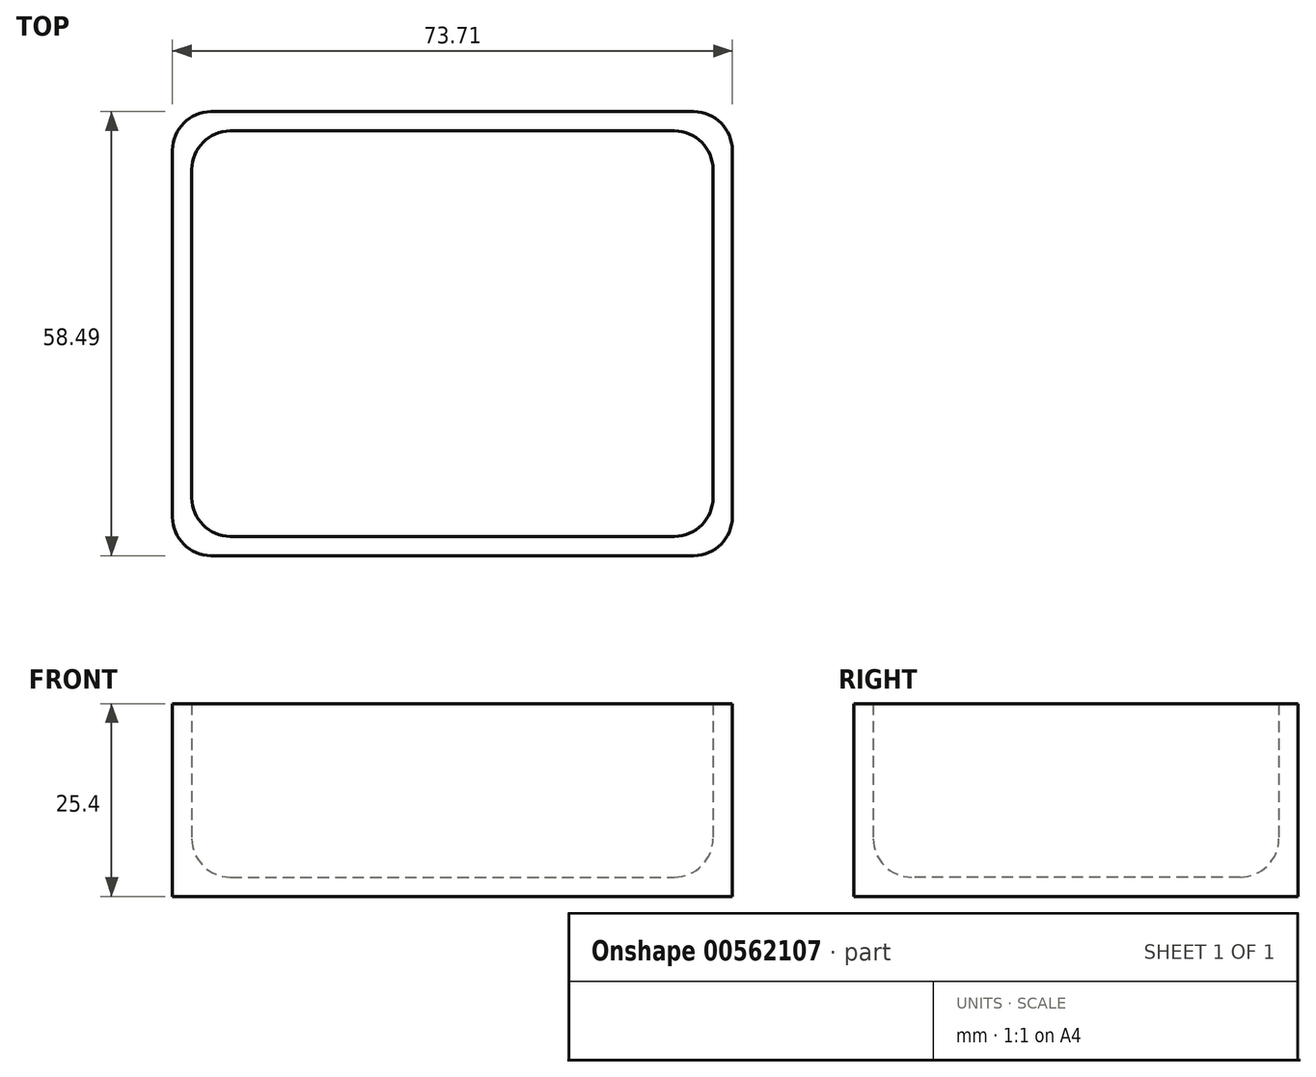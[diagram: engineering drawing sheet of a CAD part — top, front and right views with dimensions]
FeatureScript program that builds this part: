
annotation { "Feature Type Name" : "Feature", "Feature Type Description" : "" }
export const myFeature = defineFeature(function(context is Context, id is Id, definition is map)
    precondition{}
    {
        {
            var Q0;
            Q0=qCreatedBy(makeId("Top.planeOp"),FACE);
            var sketch = newSketch(context, id + "F0", { "sketchPlane" : qUnion([Q0])});
            skLineSegment(sketch, "E0.bottom", {"start": v(0, 0) * mm, "end": v(73.7, 0) * mm});
            skLineSegment(sketch, "E0.top", {"start": v(0, -58.49) * mm, "end": v(73.7, -58.49) * mm});
            skLineSegment(sketch, "E0.left", {"start": v(0, 0) * mm, "end": v(0, -58.49) * mm});
            skLineSegment(sketch, "E0.right", {"start": v(73.7, 0) * mm, "end": v(73.7, -58.49) * mm});
            skSolve(sketch);
        }
        {
            var Q0;
            Q0 = qSketchRegion(id + "F0", true);
            var Q1;
            Q1=makeQuery(id+"F0.imprint","IMPRINT",FACE,{"disambiguationData":[TD([[makeQuery(id+"F0.imprint","IMPRINT",EDGE,{"derivedFrom":sQuery(id+"F0.wireOp",EDGE,"E0.bottom")}),-1.0]])]});
            extrude(context, id + "F1", {"entities" : qUnion([Q0, Q1]), "depth" : 25.4 * mm, "offsetDistance" : 25.4 * mm});
        }
        {
            var Q0;
            Q0=makeQuery(id+"F1.opExtrude","CAP_FACE",FACE,{"disambiguationData":[OSD([sQuery(id+"F0.wireOp",EDGE,"E0.bottom"),sQuery(id+"F0.wireOp",EDGE,"E0.top"),sQuery(id+"F0.wireOp",EDGE,"E0.left"),sQuery(id+"F0.wireOp",EDGE,"E0.right")])],"isStart":false});
            shell(context, id + "F2", {"entities" : qUnion([Q0]), "thickness" : 2.54 * mm});
        }
        {
            var Q0;
            Q0=makeQuery(id+"F1.opExtrude","SWEPT_EDGE",EDGE,{"disambiguationData":[OSD([sQuery(id+"F0.wireOp",EDGE,"E0.top"),sQuery(id+"F0.wireOp",EDGE,"E0.left")])]});
            var Q1;
            Q1=makeQuery(id+"F1.opExtrude","SWEPT_EDGE",EDGE,{"disambiguationData":[OSD([sQuery(id+"F0.wireOp",EDGE,"E0.bottom"),sQuery(id+"F0.wireOp",EDGE,"E0.left")])]});
            var Q2;
            Q2=makeQuery(id+"F2.opShell","OFFSET_EDGE",EDGE,{"disambiguationData":[OSD([sQuery(id+"F0.wireOp",EDGE,"E0.top"),sQuery(id+"F0.wireOp",EDGE,"E0.left")])]});
            var Q3;
            Q3=makeQuery(id+"F2.opShell","OFFSET_EDGE",EDGE,{"disambiguationData":[OSD([sQuery(id+"F0.wireOp",EDGE,"E0.bottom"),sQuery(id+"F0.wireOp",EDGE,"E0.left")])]});
            var Q4;
            Q4=makeQuery(id+"F1.opExtrude","SWEPT_EDGE",EDGE,{"disambiguationData":[OSD([sQuery(id+"F0.wireOp",EDGE,"E0.bottom"),sQuery(id+"F0.wireOp",EDGE,"E0.right")])]});
            var Q5;
            Q5=makeQuery(id+"F2.opShell","OFFSET_EDGE",EDGE,{"disambiguationData":[OSD([sQuery(id+"F0.wireOp",EDGE,"E0.bottom"),sQuery(id+"F0.wireOp",EDGE,"E0.right")])]});
            var Q6;
            Q6=makeQuery(id+"F2.opShell","OFFSET_EDGE",EDGE,{"disambiguationData":[OSD([sQuery(id+"F0.wireOp",EDGE,"E0.top"),sQuery(id+"F0.wireOp",EDGE,"E0.right")])]});
            var Q7;
            Q7=makeQuery(id+"F1.opExtrude","SWEPT_EDGE",EDGE,{"disambiguationData":[OSD([sQuery(id+"F0.wireOp",EDGE,"E0.top"),sQuery(id+"F0.wireOp",EDGE,"E0.right")])]});
            fillet(context, id + "F3", {"entities" : qUnion([Q0, Q1, Q2, Q3, Q4, Q5, Q6, Q7]), "radius" : 5.08 * mm, "tangentPropagation" : true, "allowEdgeOverflow" : false});
        }
        {
            var Q0;
            {var subQ0=sQuery(id+"F0.wireOp",EDGE,"E0.right");Q0=makeQuery(id+"F2.opShell","OFFSET_EDGE",EDGE,{"disambiguationData":[OSD([subQ0]),TDD([makeQuery(id+"F1.opExtrude","CAP_EDGE",EDGE,{"disambiguationData":[OSD([subQ0])],"isStart":true})])]});}
            fillet(context, id + "F4", {"entities" : qUnion([Q0]), "radius" : 5.08 * mm, "tangentPropagation" : true, "allowEdgeOverflow" : false});
        }
    });
